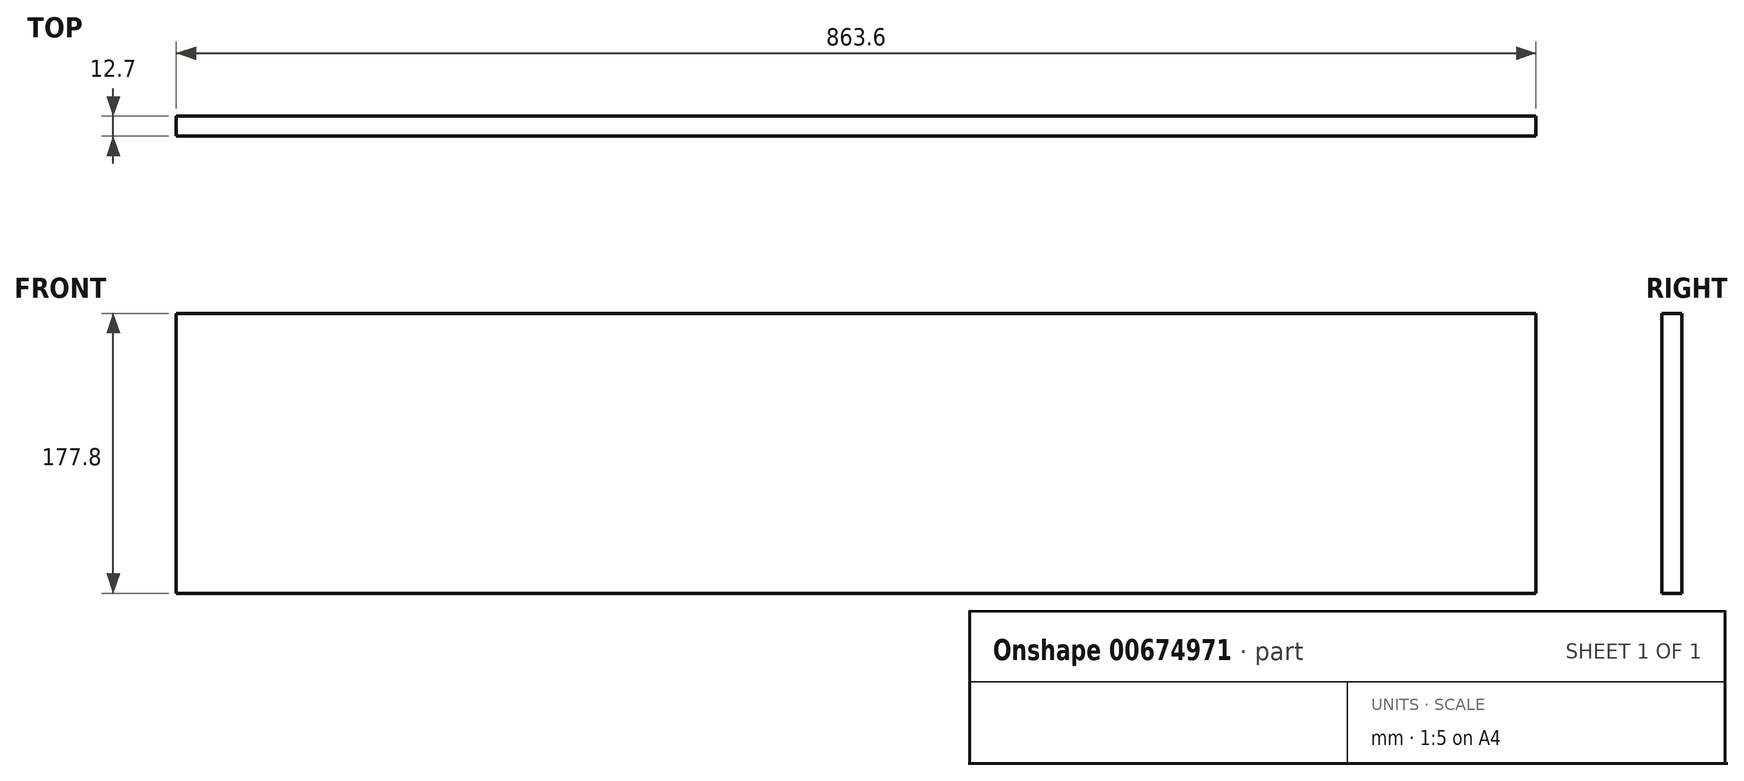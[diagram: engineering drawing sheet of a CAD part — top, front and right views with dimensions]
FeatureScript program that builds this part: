
annotation { "Feature Type Name" : "Feature", "Feature Type Description" : "" }
export const myFeature = defineFeature(function(context is Context, id is Id, definition is map)
    precondition{}
    {
        {
            var Q0;
            Q0=qCreatedBy(makeId("Front.planeOp"),FACE);
            var sketch = newSketch(context, id + "F0", { "sketchPlane" : qUnion([Q0])});
            skLineSegment(sketch, "E0.bottom", {"start": v(0, 0) * mm, "end": v(863.6, 0) * mm});
            skLineSegment(sketch, "E0.top", {"start": v(0, 177.8) * mm, "end": v(863.6, 177.8) * mm});
            skLineSegment(sketch, "E0.left", {"start": v(0, 0) * mm, "end": v(0, 177.8) * mm});
            skLineSegment(sketch, "E0.right", {"start": v(863.6, 0) * mm, "end": v(863.6, 177.8) * mm});
            skSolve(sketch);
        }
        {
            var Q0;
            Q0 = qSketchRegion(id + "F0", true);
            extrude(context, id + "F1", {"entities" : qUnion([Q0]), "depth" : 12.7 * mm, "offsetDistance" : 25.4 * mm});
        }
    });
